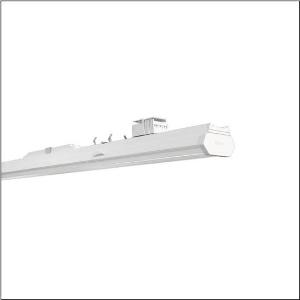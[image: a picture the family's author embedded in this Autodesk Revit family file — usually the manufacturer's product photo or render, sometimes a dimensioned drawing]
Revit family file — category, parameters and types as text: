
# Revit family: licross_r__11_protected_ho_51td13dn4f5s_2531
name_source: partatom
category: Lighting Fixtures
units: mm (PartAtom-declared; Revit-internal decimal feet)

## family parameters
Cut with Voids When Loaded = No
Host = Face
Light Source = No
Part Type = Normal
Room Calculation Point = No
Round Connector Dimension = Use Diameter
Shared = No

## types (1)
- --- (1 x LED, 15550 lm, 87.3 W, 4000K)
    Apparent Load = 87 VA
    CIE Flux Codes = 89 96 99 100 99
    Color Rendering = 80
    Color Temperature = 4000K
    Default Elevation = 1800 mm
    Description = Licross® 11 Protected HO, luminaire insert, of sheet steel, galvanised, coil coated, white, length: 1.500mm, width: 90mm, height: 101mm, LED rated luminous flux: 15.550lm, light colour: 840, SDCM (Standard Deviation of Colour Matching)MacAdam ≤ 2 SDCM (initial), control gear: DALI 2, with plug, 5-pole, with phase selection, mains connection: 220..240V, AC, 50/60Hz, rated input power: 87W, internal wiring halogen-free, primary light control with lens, of plastic, primary optical cover: cover, of PMMA, light emission: direct distribution, primary light characteristic: symmetric, protection rating (complete): IP54, insulation class (complete): insulation class I (protective earthing), certification: CE, ENEC, VDE, UKCA, protection symbol: D if used in an environment with non-conductive dust loads with corresponding accessories, impact resistance: IK06, permissible ambient temperature for indoor applications: -25..+30°C, corresponds to IFS (International Featured Standards) requirements for safety and quality in the food industry, reducing of maximum allowable ambient temperature of 5°C with ceiling mounting, LABS conformity tested according to VDMA 24364:2018-05, packaging unit: 1 piece
    Height = 92 mm
    Lamp = 1 x LED
    Lamp Light Flux = 15550 lm
    Lamp Power = 87.3 W
    Lamp count = 1
    Length = 1500 mm
    Luminous efficacy = 178 lm/W
    Manufacturer = Siteco
    ModVariant = No
    Model = 51TD13DN4F5S
    Mounting Place = Ceiling
    Mounting Type = Pendant
    Number of Poles = 1
    OnlyDefault = Yes
    Power Factor = 1
    Product Name = Licross® 11 Protected HO
    Product group = luminaire insert | ceiling pendant
    ProductGroupID = 901
    Protection Class = Protection class I
    Protection Degree = IP 54
    RLX_Detail_Level = 1
    RLX_Emergency_Light_Flux = 0 lm
    RLX_Emergency_Type = 0
    RLX_Emergency_Type_DB = No
    RlxData = <blob elided: 24505 chars, md5=2d927526>
    Socket = socket
    Standby Power = 0 W
    System Light Flux = 15550 lm
    System Power = 87 W
    Type Comments = factory setting: luminous flux: 100 % | dim-lin: 254 | 589 mA
    Type Image = l_1256145.jpg
    URL = http://relux.com
    VarID = @adj_106431
    Voltage = 0 V
    Weight = 0.00 kg
    Width = 88 mm

## geometry (parser evidence)
native form markers: Blend x4, Sweep x11
no freeform markers — native parametric forms only
